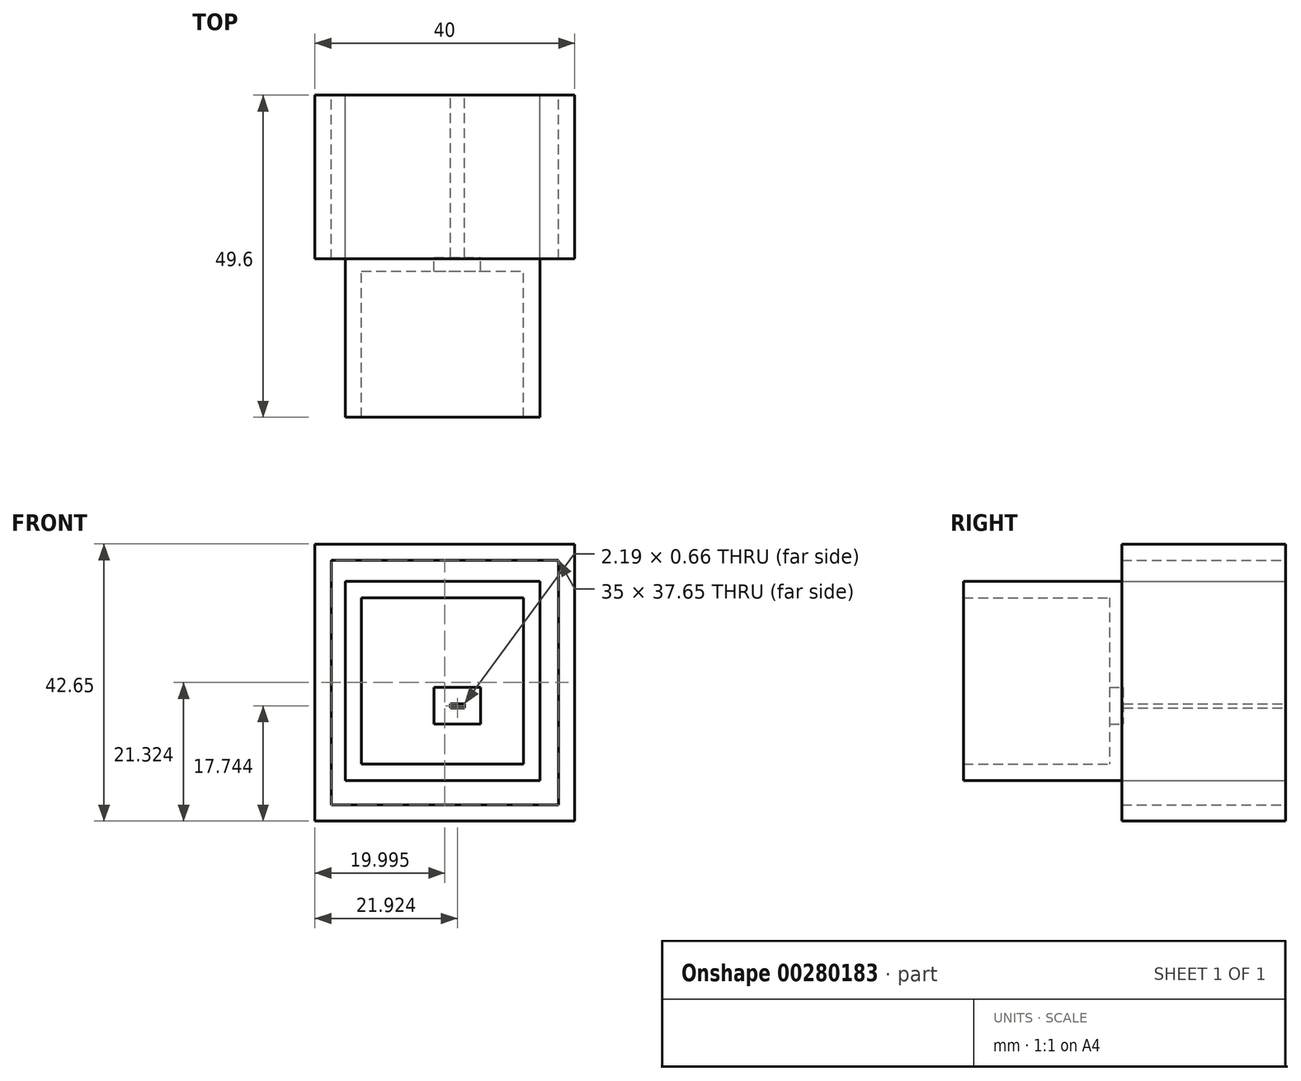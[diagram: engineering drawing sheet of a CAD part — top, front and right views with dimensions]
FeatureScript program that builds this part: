
annotation { "Feature Type Name" : "Feature", "Feature Type Description" : "" }
export const myFeature = defineFeature(function(context is Context, id is Id, definition is map)
    precondition{}
    {
        {
            var Q0;
            Q0=qCreatedBy(makeId("Front.planeOp"),FACE);
            var sketch = newSketch(context, id + "F0", { "sketchPlane" : qUnion([Q0])});
            skLineSegment(sketch, "E0.bottom", {"start": v(-61.08, 57.39) * mm, "end": v(-21.08, 57.39) * mm});
            skLineSegment(sketch, "E0.top", {"start": v(-61.08, 14.74) * mm, "end": v(-21.08, 14.74) * mm});
            skLineSegment(sketch, "E0.left", {"start": v(-61.08, 57.39) * mm, "end": v(-61.08, 14.74) * mm});
            skLineSegment(sketch, "E0.right", {"start": v(-21.08, 57.39) * mm, "end": v(-21.08, 14.74) * mm});
            skSolve(sketch);
        }
        {
            var Q0;
            Q0=makeQuery(id+"F0.imprint","IMPRINT",FACE,{"disambiguationData":[TD([[makeQuery(id+"F0.imprint","IMPRINT",EDGE,{"derivedFrom":sQuery(id+"F0.wireOp",EDGE,"E0.bottom")}),-1.0]])]});
            extrude(context, id + "F1", {"entities" : qUnion([Q0]), "depth" : 0.2 * mm});
        }
        {
            var Q0;
            Q0=makeQuery(id+"F1.opExtrude","CAP_FACE",FACE,{"disambiguationData":[OSD([sQuery(id+"F0.wireOp",EDGE,"E0.bottom"),sQuery(id+"F0.wireOp",EDGE,"E0.top"),sQuery(id+"F0.wireOp",EDGE,"E0.left"),sQuery(id+"F0.wireOp",EDGE,"E0.right")])],"isStart":false});
            extrude(context, id + "F2", {"entities" : qUnion([Q0]), "operationType" : NewBodyOperationType.ADD, "depth" : 25 * mm});
        }
        {
            var Q0;
            Q0=makeQuery(id+"F1.opExtrude","CAP_FACE",FACE,{"disambiguationData":[OSD([sQuery(id+"F0.wireOp",EDGE,"E0.bottom"),sQuery(id+"F0.wireOp",EDGE,"E0.top"),sQuery(id+"F0.wireOp",EDGE,"E0.left"),sQuery(id+"F0.wireOp",EDGE,"E0.right")])],"isStart":true});
            var Q1;
            Q1=makeQuery(id+"F2.opExtrude","CAP_FACE",FACE,{"disambiguationData":[OSD([sQuery(id+"F0.wireOp",EDGE,"E0.bottom"),sQuery(id+"F0.wireOp",EDGE,"E0.top"),sQuery(id+"F0.wireOp",EDGE,"E0.left"),sQuery(id+"F0.wireOp",EDGE,"E0.right")])],"isStart":false});
            shell(context, id + "F3", {"entities" : qUnion([Q0, Q1]), "thickness" : 2.5 * mm});
        }
        {
            var Q0;
            Q0=qCreatedBy(makeId("Front.planeOp"),FACE);
            var sketch = newSketch(context, id + "F4", { "sketchPlane" : qUnion([Q0])});
            skLineSegment(sketch, "E1.bottom", {"start": v(-56.44, 51.63) * mm, "end": v(-26.47, 51.63) * mm});
            skLineSegment(sketch, "E1.top", {"start": v(-56.44, 21) * mm, "end": v(-26.47, 21) * mm});
            skLineSegment(sketch, "E1.left", {"start": v(-56.44, 51.63) * mm, "end": v(-56.44, 21) * mm});
            skLineSegment(sketch, "E1.right", {"start": v(-26.47, 51.63) * mm, "end": v(-26.47, 21) * mm});
            skLineSegment(sketch, "E2.bottom", {"start": v(-40.25, 32.81) * mm, "end": v(-38.06, 32.81) * mm});
            skLineSegment(sketch, "E2.top", {"start": v(-40.25, 32.16) * mm, "end": v(-38.06, 32.16) * mm});
            skLineSegment(sketch, "E2.left", {"start": v(-40.25, 32.81) * mm, "end": v(-40.25, 32.16) * mm});
            skLineSegment(sketch, "E2.right", {"start": v(-38.06, 32.81) * mm, "end": v(-38.06, 32.16) * mm});
            skSolve(sketch);
        }
        {
            var Q0;
            Q0 = qSketchRegion(id + "F4", true);
            extrude(context, id + "F5", {"entities" : qUnion([Q0]), "depth" : 25 * mm});
        }
        {
            var Q0;
            Q0=makeQuery(id+"F5.opExtrude","CAP_FACE",FACE,{"disambiguationData":[OSD([sQuery(id+"F4.wireOp",EDGE,"E1.bottom"),sQuery(id+"F4.wireOp",EDGE,"E1.top"),sQuery(id+"F4.wireOp",EDGE,"E1.left"),sQuery(id+"F4.wireOp",EDGE,"E1.right"),sQuery(id+"F4.wireOp",EDGE,"E2.bottom"),sQuery(id+"F4.wireOp",EDGE,"E2.top"),sQuery(id+"F4.wireOp",EDGE,"E2.left"),sQuery(id+"F4.wireOp",EDGE,"E2.right")])],"isStart":false});
            shell(context, id + "F6", {"entities" : qUnion([Q0]), "thickness" : 2.5 * mm});
        }
        {
            var Q0;
            Q0=makeQuery(id+"F5.opExtrude","CAP_FACE",FACE,{"disambiguationData":[OSD([sQuery(id+"F4.wireOp",EDGE,"E1.bottom"),sQuery(id+"F4.wireOp",EDGE,"E1.top"),sQuery(id+"F4.wireOp",EDGE,"E1.left"),sQuery(id+"F4.wireOp",EDGE,"E1.right"),sQuery(id+"F4.wireOp",EDGE,"E2.bottom"),sQuery(id+"F4.wireOp",EDGE,"E2.top"),sQuery(id+"F4.wireOp",EDGE,"E2.left"),sQuery(id+"F4.wireOp",EDGE,"E2.right")])],"isStart":false});
            var Q1;
            {var subQ0=sQuery(id+"F4.wireOp",EDGE,"E2.right");var subQ1=sQuery(id+"F4.wireOp",EDGE,"E2.left");var subQ2=sQuery(id+"F4.wireOp",EDGE,"E2.top");var subQ3=sQuery(id+"F4.wireOp",EDGE,"E2.bottom");var subQ4=sQuery(id+"F4.wireOp",EDGE,"E1.right");var subQ5=sQuery(id+"F4.wireOp",EDGE,"E1.left");var subQ6=sQuery(id+"F4.wireOp",EDGE,"E1.top");var subQ7=sQuery(id+"F4.wireOp",EDGE,"E1.bottom");Q1=makeQuery(id+"F6.opShell","OFFSET_FACE",FACE,{"disambiguationData":[OSD([subQ7,subQ6,subQ5,subQ4,subQ3,subQ2,subQ1,subQ0]),TDD([makeQuery(id+"F5.opExtrude","CAP_FACE",FACE,{"disambiguationData":[OSD([subQ7,subQ6,subQ5,subQ4,subQ3,subQ2,subQ1,subQ0])],"isStart":true})])]});}
            extrude(context, id + "F7", {"entities" : qUnion([Q0, Q1]), "operationType" : NewBodyOperationType.ADD, "depth" : 24.6 * mm});
        }
    });
